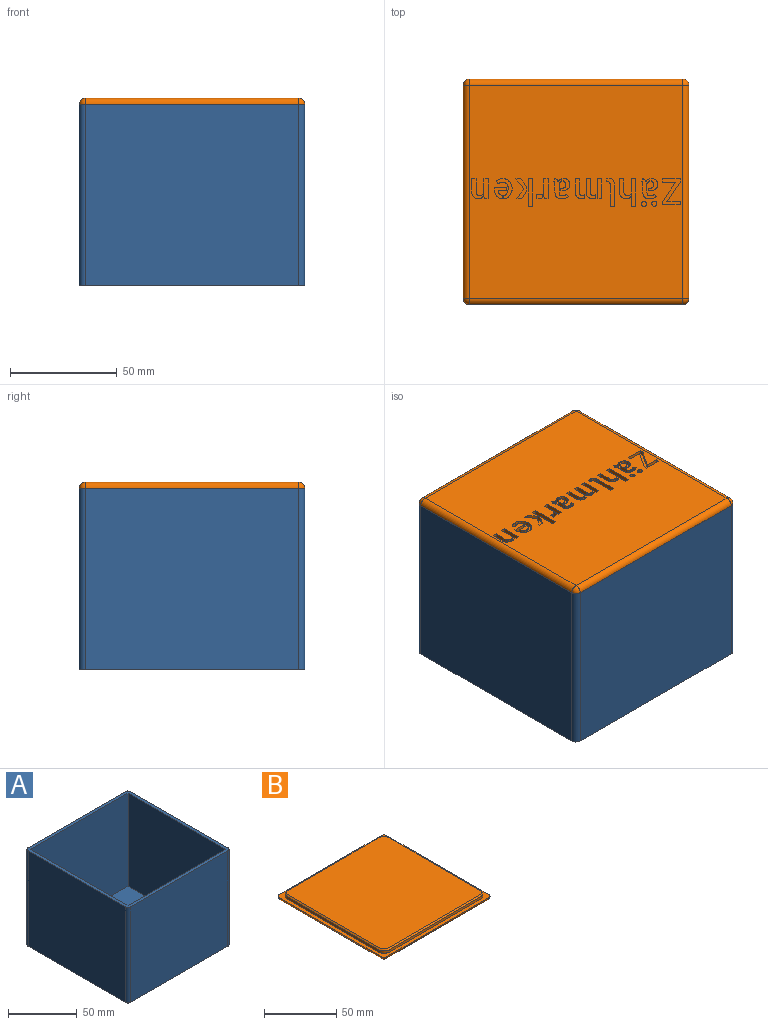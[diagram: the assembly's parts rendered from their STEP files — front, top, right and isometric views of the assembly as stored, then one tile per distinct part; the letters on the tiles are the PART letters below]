
ASSEMBLY  parts=2 mates=1
PART A: 15 faces, bbox 105.6x105.6x85 mm
  f0: plane 105.6x105.6mm, normal (0,0,-1), area 11144.6mm2, adj f5,f6,f7,f8,f9,f10,f11,f12
  f1: plane 100x83mm, normal (-1,0,0), area 8300mm2, adj f2,f4,f13,f14
  f2: plane 100x83mm, normal (0,-1,0), area 8300mm2, adj f1,f3,f13,f14
  f3: plane 100x83mm, normal (1,0,0), area 8300mm2, adj f2,f4,f13,f14
  f4: plane 100x83mm, normal (0,1,0), area 8300mm2, adj f1,f3,f13,f14
  f5: cylinder r=2.8mm len=85mm, axis (0,0,-1), area 373.8mm2, adj f0,f6,f12,f13
  f6: plane 100x85mm, normal (-1,0,0), area 8500mm2, adj f0,f5,f7,f13
  f7: cylinder r=2.8mm len=85mm, axis (0,0,-1), area 373.8mm2, adj f0,f6,f8,f13
  f8: plane 100x85mm, normal (0,-1,0), area 8500mm2, adj f0,f7,f9,f13
  f9: cylinder r=2.8mm len=85mm, axis (0,0,-1), area 373.8mm2, adj f0,f8,f10,f13
  f10: plane 100x85mm, normal (1,0,0), area 8500mm2, adj f0,f9,f11,f13
  f11: cylinder r=2.8mm len=85mm, axis (0,0,-1), area 373.8mm2, adj f0,f10,f12,f13
  f12: plane 100x85mm, normal (0,1,0), area 8500mm2, adj f0,f5,f11,f13
  f13: plane 105.6x105.6mm, normal (0,0,1), area 1144.6mm2, adj f1,f2,f3,f4,f5,f6,f7,f8
  f14: plane 100x100mm, normal (0,0,1), area 10000mm2, adj f1,f2,f3,f4
PART B: 344 faces, bbox 105.6x105.6x5.8 mm
  f0: extruded ~1.8x0.65mm, area 1.4mm2, adj f1,f295,f309,f323
  f1: extruded ~1.8x1.03mm, area 2.4mm2, adj f0,f2,f309,f323
  f2: extruded ~1.8x1.26mm, area 2.4mm2, adj f1,f3,f309,f323
  f3: extruded ~1.8x1.02mm, area 1.9mm2, adj f2,f4,f309,f323
  f4: extruded ~1.8x0.97mm, area 1.9mm2, adj f3,f5,f309,f323
  f5: plane 1.8x1.27mm, normal (-1,0,0), area 2.3mm2, adj f4,f6,f309,f323
  f6: extruded ~1.8x0.75mm, area 1.4mm2, adj f5,f7,f309,f323
  f7: extruded ~1.8x0.62mm, area 1.1mm2, adj f6,f8,f309,f323
  f8: extruded ~1.8x0.88mm, area 1.7mm2, adj f7,f9,f309,f323
  f9: extruded ~1.8x0.62mm, area 1.4mm2, adj f8,f10,f309,f323
  f10: extruded ~1.8x0.91mm, area 1.7mm2, adj f9,f11,f309,f323
  f11: extruded ~1.8x1.07mm, area 1.9mm2, adj f10,f12,f309,f323
  f12: plane 5.07x1.8mm, normal (-1,0,0), area 9.1mm2, adj f11,f13,f309,f323
  f13: plane 2.01x1.8mm, normal (0,1,0), area 3.6mm2, adj f12,f14,f309,f323
  f14: plane 5.24x1.8mm, normal (1,0,0), area 9.4mm2, adj f13,f15,f309,f323
  f15: extruded ~1.8x0.81mm, area 1.5mm2, adj f14,f16,f309,f323
  f16: extruded ~1.8x0.82mm, area 1.5mm2, adj f15,f295,f309,f323
  f17: plane 1.8x0.94mm, normal (0.98,-0.22,0), area 1.7mm2, adj f18,f275,f309,f343
  f18: plane 1.8x1.78mm, normal (0,-1,0), area 3.2mm2, adj f17,f19,f309,f343
  f19: plane 9.32x1.8mm, normal (-1,0,0), area 16.8mm2, adj f18,f20,f309,f343
  f20: plane 2x1.8mm, normal (0,1,0), area 3.6mm2, adj f19,f275,f309,f343
  f21: extruded ~1.8x0.45mm, area 0.8mm2, adj f22,f276,f309,f342
  f22: extruded ~1.8x1.18mm, area 2.2mm2, adj f21,f23,f309,f342
  f23: extruded ~1.8x0.82mm, area 1.9mm2, adj f22,f24,f309,f342
  f24: extruded ~1.8x0.96mm, area 1.9mm2, adj f23,f25,f309,f342
  f25: extruded ~1.8x1.2mm, area 2.2mm2, adj f24,f26,f309,f342
  f26: extruded ~1.8x0.88mm, area 1.6mm2, adj f25,f27,f309,f342
  f27: extruded ~1.8x1mm, area 1.9mm2, adj f26,f28,f309,f342
  f28: extruded ~1.8x0.87mm, area 1.9mm2, adj f27,f29,f309,f342
  f29: extruded ~1.8x1.01mm, area 2.1mm2, adj f28,f30,f309,f342
  f30: plane 1.8x1.59mm, normal (1,0,0), area 2.9mm2, adj f29,f31,f309,f342
  f31: extruded ~1.8x1.51mm, area 2.9mm2, adj f30,f32,f309,f342
  f32: extruded ~1.8x1.23mm, area 2.9mm2, adj f31,f33,f309,f342
  f33: extruded ~1.8x1.48mm, area 3.1mm2, adj f32,f34,f309,f342
  f34: extruded ~1.8x1.78mm, area 3.3mm2, adj f33,f35,f309,f342
  f35: extruded ~1.85x1.8mm, area 3.4mm2, adj f34,f36,f309,f342
  f36: extruded ~1.8x1.5mm, area 3.2mm2, adj f35,f37,f309,f342
  f37: extruded ~1.8x1.35mm, area 3.1mm2, adj f36,f38,f309,f342
  f38: extruded ~1.8x1.7mm, area 3.2mm2, adj f37,f39,f309,f342
  f39: extruded ~1.85x1.8mm, area 3.4mm2, adj f38,f40,f309,f342
  f40: extruded ~1.8x1.27mm, area 3mm2, adj f39,f41,f309,f342
  f41: plane 1.8x1.11mm, normal (0.84,-0.55,0), area 2.4mm2, adj f40,f42,f309,f342
  f42: extruded ~1.8x0.54mm, area 1.2mm2, adj f41,f43,f309,f342
  f43: extruded ~1.8x0.61mm, area 1.2mm2, adj f42,f276,f309,f342
  f44: extruded ~1.8x1.61mm, area 3mm2, adj f45,f277,f309,f341
  f45: plane 1.8x1.55mm, normal (-1,0,0), area 2.8mm2, adj f44,f46,f309,f341
  f46: extruded ~1.8x0.81mm, area 1.6mm2, adj f45,f47,f309,f341
  f47: extruded ~1.8x0.64mm, area 1.5mm2, adj f46,f48,f309,f341
  f48: extruded ~1.8x0.73mm, area 1.5mm2, adj f47,f49,f309,f341
  f49: extruded ~1.8x0.83mm, area 1.5mm2, adj f48,f50,f309,f341
  f50: plane 3.81x1.8mm, normal (0,-1,0), area 6.9mm2, adj f49,f51,f309,f341
  f51: plane 1.8x1.45mm, normal (-1,0,0), area 2.6mm2, adj f50,f52,f309,f341
  f52: plane 5.66x1.8mm, normal (0,1,0), area 10.2mm2, adj f51,f53,f309,f341
  f53: extruded ~1.8x0.79mm, area 1.4mm2, adj f52,f54,f309,f341
  f54: extruded ~1.8x1.69mm, area 3.1mm2, adj f53,f55,f309,f341
  f55: extruded ~1.8x1.44mm, area 3mm2, adj f54,f277,f309,f341
  f56: plane 12.84x1.8mm, normal (-1,0,0), area 23.1mm2, adj f57,f278,f309,f340
  f57: plane 2.01x1.8mm, normal (0,1,0), area 3.6mm2, adj f56,f58,f309,f340
  f58: plane 12.84x1.8mm, normal (1,0,0), area 23.1mm2, adj f57,f278,f309,f340
  f59: plane 4.68x3.7mm, normal (0.78,-0.62,0), area 10.7mm2, adj f60,f279,f309,f339
  f60: plane 4.64x3.27mm, normal (0.82,0.58,0), area 10.2mm2, adj f59,f61,f309,f339
  f61: plane 2.25x1.8mm, normal (0,-1,0), area 4mm2, adj f60,f62,f309,f339
  f62: plane 3.45x2.31mm, normal (-0.83,-0.56,0), area 7.5mm2, adj f61,f63,f309,f339
  f63: plane 2.3x1.8mm, normal (-1,0,0), area 4.1mm2, adj f62,f64,f309,f339
  f64: plane 3.57x2.71mm, normal (-0.8,0.6,0), area 8.1mm2, adj f63,f279,f309,f339
  f65: extruded ~1.8x0.99mm, area 1.9mm2, adj f66,f280,f309,f338
  f66: plane 1.8x1.69mm, normal (-1,0,0), area 3mm2, adj f65,f67,f309,f338
  f67: extruded ~1.8x0.7mm, area 1.3mm2, adj f66,f68,f309,f338
  f68: extruded ~1.8x0.74mm, area 1.3mm2, adj f67,f69,f309,f338
  f69: extruded ~1.8x1.12mm, area 2mm2, adj f68,f70,f309,f338
  f70: plane 2.08x1.8mm, normal (1,0,0), area 3.7mm2, adj f69,f280,f309,f338
  f71: plane 1.8x0.96mm, normal (0.98,-0.22,0), area 1.8mm2, adj f72,f281,f309,f337
  f72: plane 1.8x1.78mm, normal (0,-1,0), area 3.2mm2, adj f71,f73,f309,f337
  f73: plane 9.32x1.8mm, normal (-1,0,0), area 16.8mm2, adj f72,f74,f309,f337
  f74: plane 2x1.8mm, normal (0,1,0), area 3.6mm2, adj f73,f281,f309,f337
  f75: extruded ~1.8x0.39mm, area 0.7mm2, adj f76,f282,f309,f336
  f76: plane 2.28x1.8mm, normal (1,0,0), area 4.1mm2, adj f75,f77,f309,f336
  f77: extruded ~1.8x1.17mm, area 2.1mm2, adj f76,f78,f309,f336
  f78: extruded ~1.8x1.17mm, area 2.1mm2, adj f77,f79,f309,f336
  f79: extruded ~1.8x0.96mm, area 1.9mm2, adj f78,f80,f309,f336
  f80: extruded ~1.8x0.68mm, area 1.7mm2, adj f79,f81,f309,f336
  f81: extruded ~1.8x0.86mm, area 1.7mm2, adj f80,f82,f309,f336
  f82: extruded ~1.8x0.97mm, area 1.8mm2, adj f81,f83,f309,f336
  f83: extruded ~1.8x1.05mm, area 1.9mm2, adj f82,f84,f309,f336
  f84: extruded ~1.8x0.93mm, area 1.7mm2, adj f83,f85,f309,f336
  f85: extruded ~1.8x0.76mm, area 1.5mm2, adj f84,f86,f309,f336
  f86: extruded ~1.8x0.49mm, area 1.1mm2, adj f85,f87,f309,f336
  f87: plane 1.8x1.14mm, normal (-0.84,0.55,0), area 2.4mm2, adj f86,f88,f309,f336
  f88: extruded ~1.8x0.31mm, area 0.7mm2, adj f87,f89,f309,f336
  f89: extruded ~1.8x0.48mm, area 1mm2, adj f88,f90,f309,f336
  f90: extruded ~1.8x0.59mm, area 1.1mm2, adj f89,f91,f309,f336
  f91: extruded ~1.8x0.68mm, area 1.2mm2, adj f90,f92,f309,f336
  f92: extruded ~1.8x0.69mm, area 1.2mm2, adj f91,f93,f309,f336
  f93: extruded ~1.8x0.49mm, area 1mm2, adj f92,f94,f309,f336
  f94: extruded ~1.8x0.7mm, area 1.4mm2, adj f93,f95,f309,f336
  f95: extruded ~1.8x1.29mm, area 2.3mm2, adj f94,f96,f309,f336
  f96: plane 3.49x1.8mm, normal (-1,0,0), area 6.3mm2, adj f95,f97,f309,f336
  f97: extruded ~1.8x0.57mm, area 1.4mm2, adj f96,f98,f309,f336
  f98: extruded ~1.8x0.72mm, area 1.4mm2, adj f97,f99,f309,f336
  f99: plane 1.8x1.26mm, normal (-1,0,0), area 2.3mm2, adj f98,f100,f309,f336
  f100: extruded ~1.8x1.08mm, area 2.1mm2, adj f99,f101,f309,f336
  f101: extruded ~1.8x0.73mm, area 1.8mm2, adj f100,f102,f309,f336
  f102: extruded ~1.8x0.49mm, area 1mm2, adj f101,f103,f309,f336
  f103: extruded ~1.8x0.4mm, area 1mm2, adj f102,f104,f309,f336
  f104: extruded ~1.8x0.46mm, area 1mm2, adj f103,f105,f309,f336
  f105: extruded ~1.8x0.45mm, area 0.8mm2, adj f104,f106,f309,f336
  f106: plane 1.8x1.11mm, normal (0.9,0.43,0), area 2.2mm2, adj f105,f107,f309,f336
  f107: extruded ~1.8x0.29mm, area 0.7mm2, adj f106,f108,f309,f336
  f108: extruded ~1.8x0.48mm, area 0.9mm2, adj f107,f282,f309,f336
  f109: extruded ~1.8x1.11mm, area 2.1mm2, adj f110,f283,f309,f335
  f110: extruded ~1.8x0.87mm, area 1.6mm2, adj f109,f111,f309,f335
  f111: extruded ~1.8x0.52mm, area 1.3mm2, adj f110,f112,f309,f335
  f112: extruded ~1.8x0.68mm, area 1.3mm2, adj f111,f113,f309,f335
  f113: extruded ~1.8x0.69mm, area 1.3mm2, adj f112,f114,f309,f335
  f114: plane 1.8x0.36mm, normal (0,1,0), area 0.7mm2, adj f113,f115,f309,f335
  f115: plane 1.8x1.17mm, normal (1,0,0), area 2.1mm2, adj f114,f116,f309,f335
  f116: plane 1.8x0.73mm, normal (0,-1,0), area 1.3mm2, adj f115,f117,f309,f335
  f117: extruded ~1.8x1.3mm, area 2.4mm2, adj f116,f118,f309,f335
  f118: extruded ~1.8x1.15mm, area 2.3mm2, adj f117,f119,f309,f335
  f119: extruded ~1.8x0.91mm, area 2.2mm2, adj f118,f120,f309,f335
  f120: extruded ~1.8x1.31mm, area 2.5mm2, adj f119,f121,f309,f335
  f121: extruded ~1.8x1.34mm, area 2.5mm2, adj f120,f122,f309,f335
  f122: extruded ~1.8x0.88mm, area 2mm2, adj f121,f123,f309,f335
  f123: extruded ~1.8x0.92mm, area 1.9mm2, adj f122,f124,f309,f335
  f124: extruded ~1.8x1.08mm, area 2mm2, adj f123,f125,f309,f335
  f125: extruded ~1.8x0.21mm, area 0.4mm2, adj f124,f126,f309,f335
  f126: plane 1.8x1.34mm, normal (1,0,0), area 2.4mm2, adj f125,f283,f309,f335
  f127: extruded ~1.8x0.63mm, area 1.3mm2, adj f128,f284,f309,f334
  f128: extruded ~1.8x1.02mm, area 2.5mm2, adj f127,f129,f309,f334
  f129: extruded ~1.8x1.28mm, area 2.4mm2, adj f128,f130,f309,f334
  f130: extruded ~1.8x0.9mm, area 1.7mm2, adj f129,f131,f309,f334
  f131: extruded ~1.8x0.85mm, area 1.7mm2, adj f130,f132,f309,f334
  f132: plane 1.8x1.31mm, normal (-1,0,0), area 2.4mm2, adj f131,f133,f309,f334
  f133: extruded ~1.8x0.77mm, area 1.5mm2, adj f132,f134,f309,f334
  f134: extruded ~1.8x0.59mm, area 1.1mm2, adj f133,f135,f309,f334
  f135: extruded ~1.8x0.68mm, area 1.3mm2, adj f134,f136,f309,f334
  f136: extruded ~1.8x0.62mm, area 1.3mm2, adj f135,f137,f309,f334
  f137: extruded ~1.8x0.9mm, area 1.6mm2, adj f136,f138,f309,f334
  f138: plane 6.14x1.8mm, normal (-1,0,0), area 11mm2, adj f137,f139,f309,f334
  f139: plane 2x1.8mm, normal (0,1,0), area 3.6mm2, adj f138,f140,f309,f334
  f140: plane 5.24x1.8mm, normal (1,0,0), area 9.4mm2, adj f139,f141,f309,f334
  f141: extruded ~1.8x0.82mm, area 1.5mm2, adj f140,f142,f309,f334
  f142: extruded ~1.8x0.75mm, area 1.4mm2, adj f141,f284,f309,f334
  f143: extruded ~1.8x1.06mm, area 2mm2, adj f144,f285,f309,f333
  f144: extruded ~1.8x0.86mm, area 1.6mm2, adj f143,f145,f309,f333
  f145: extruded ~1.8x0.91mm, area 1.8mm2, adj f144,f146,f309,f333
  f146: plane 1.8x1.31mm, normal (-1,0,0), area 2.4mm2, adj f145,f147,f309,f333
  f147: extruded ~1.8x0.88mm, area 1.7mm2, adj f146,f148,f309,f333
  f148: extruded ~1.8x0.5mm, area 0.9mm2, adj f147,f149,f309,f333
  f149: extruded ~1.8x0.69mm, area 1.3mm2, adj f148,f150,f309,f333
  f150: extruded ~1.8x0.62mm, area 1.3mm2, adj f149,f151,f309,f333
  f151: extruded ~1.8x0.9mm, area 1.6mm2, adj f150,f152,f309,f333
  f152: extruded ~1.8x1.07mm, area 1.9mm2, adj f151,f153,f309,f333
  f153: plane 5.07x1.8mm, normal (-1,0,0), area 9.1mm2, adj f152,f154,f309,f333
  f154: plane 1.98x1.8mm, normal (0,1,0), area 3.6mm2, adj f153,f155,f309,f333
  f155: plane 6.34x1.8mm, normal (1,0,0), area 11.4mm2, adj f154,f156,f309,f333
  f156: extruded ~1.8x1.23mm, area 2.3mm2, adj f155,f157,f309,f333
  f157: extruded ~1.8x0.98mm, area 2.1mm2, adj f156,f285,f309,f333
  f158: plane 1.8x0.96mm, normal (0.98,-0.22,0), area 1.8mm2, adj f159,f286,f309,f332
  f159: plane 1.8x1.8mm, normal (0,-1,0), area 3.2mm2, adj f158,f160,f309,f332
  f160: plane 9.32x1.8mm, normal (-1,0,0), area 16.8mm2, adj f159,f161,f309,f332
  f161: plane 2.01x1.8mm, normal (0,1,0), area 3.6mm2, adj f160,f286,f309,f332
  f162: extruded ~1.8x0.88mm, area 1.6mm2, adj f163,f287,f309,f331
  f163: plane 9.99x1.8mm, normal (1,0,0), area 18mm2, adj f162,f164,f309,f331
  f164: plane 2.02x1.8mm, normal (0,-1,0), area 3.6mm2, adj f163,f165,f309,f331
  f165: plane 9.89x1.8mm, normal (-1,0,0), area 17.8mm2, adj f164,f166,f309,f331
  f166: extruded ~1.8x0.7mm, area 1.3mm2, adj f165,f167,f309,f331
  f167: extruded ~1.8x0.92mm, area 1.7mm2, adj f166,f168,f309,f331
  f168: extruded ~1.8x0.85mm, area 1.8mm2, adj f167,f169,f309,f331
  f169: extruded ~1.8x0.88mm, area 1.8mm2, adj f168,f170,f309,f331
  f170: extruded ~1.8x0.45mm, area 0.8mm2, adj f169,f171,f309,f331
  f171: extruded ~1.8x0.5mm, area 0.9mm2, adj f170,f172,f309,f331
  f172: extruded ~1.8x0.49mm, area 0.9mm2, adj f171,f173,f309,f331
  f173: extruded ~1.8x0.43mm, area 0.8mm2, adj f172,f174,f309,f331
  f174: extruded ~1.8x0.44mm, area 0.8mm2, adj f173,f175,f309,f331
  f175: plane 1.8x1.22mm, normal (1,0,0), area 2.2mm2, adj f174,f176,f309,f331
  f176: extruded ~1.8x0.73mm, area 1.3mm2, adj f175,f177,f309,f331
  f177: extruded ~1.8x0.6mm, area 1.2mm2, adj f176,f287,f309,f331
  f178: extruded ~1.8x0.65mm, area 1.4mm2, adj f179,f288,f309,f330
  f179: extruded ~1.8x1.03mm, area 2.4mm2, adj f178,f180,f309,f330
  f180: extruded ~1.8x1.26mm, area 2.4mm2, adj f179,f181,f309,f330
  f181: extruded ~1.8x1.02mm, area 1.9mm2, adj f180,f182,f309,f330
  f182: extruded ~1.8x0.97mm, area 1.9mm2, adj f181,f183,f309,f330
  f183: plane 1.8x1.27mm, normal (-1,0,0), area 2.3mm2, adj f182,f184,f309,f330
  f184: extruded ~1.8x0.75mm, area 1.4mm2, adj f183,f185,f309,f330
  f185: extruded ~1.8x0.62mm, area 1.1mm2, adj f184,f186,f309,f330
  f186: extruded ~1.8x0.88mm, area 1.7mm2, adj f185,f187,f309,f330
  f187: extruded ~1.8x0.62mm, area 1.4mm2, adj f186,f188,f309,f330
  f188: extruded ~1.8x0.91mm, area 1.7mm2, adj f187,f189,f309,f330
  f189: extruded ~1.8x1.07mm, area 1.9mm2, adj f188,f190,f309,f330
  f190: plane 5.07x1.8mm, normal (-1,0,0), area 9.1mm2, adj f189,f191,f309,f330
  f191: plane 2.01x1.8mm, normal (0,1,0), area 3.6mm2, adj f190,f192,f309,f330
  f192: plane 5.24x1.8mm, normal (1,0,0), area 9.4mm2, adj f191,f193,f309,f330
  f193: extruded ~1.8x0.81mm, area 1.5mm2, adj f192,f194,f309,f330
  f194: extruded ~1.8x0.82mm, area 1.5mm2, adj f193,f288,f309,f330
  f195: plane 2x1.8mm, normal (0,-1,0), area 3.6mm2, adj f196,f289,f309,f329
  f196: plane 12.84x1.8mm, normal (-1,0,0), area 23.1mm2, adj f195,f197,f309,f329
  f197: plane 2x1.8mm, normal (0,1,0), area 3.6mm2, adj f196,f289,f309,f329
  f198: extruded ~1.8x0.84mm, area 1.7mm2, adj f199,f290,f309,f328
  f199: extruded ~1.8x0.83mm, area 1.7mm2, adj f198,f200,f309,f328
  f200: extruded ~1.8x0.84mm, area 1.7mm2, adj f199,f201,f309,f328
  f201: extruded ~1.8x0.84mm, area 1.7mm2, adj f200,f202,f309,f328
  f202: extruded ~1.8x0.83mm, area 1.7mm2, adj f201,f203,f309,f328
  f203: extruded ~1.8x0.84mm, area 1.7mm2, adj f202,f204,f309,f328
  f204: extruded ~1.8x0.84mm, area 1.7mm2, adj f203,f290,f309,f328
  f205: extruded ~1.8x0.84mm, area 1.7mm2, adj f206,f291,f309,f327
  f206: extruded ~1.8x0.83mm, area 1.7mm2, adj f205,f207,f309,f327
  f207: extruded ~1.8x0.84mm, area 1.7mm2, adj f206,f208,f309,f327
  f208: extruded ~1.8x0.84mm, area 1.7mm2, adj f207,f209,f309,f327
  f209: extruded ~1.8x0.83mm, area 1.7mm2, adj f208,f210,f309,f327
  f210: extruded ~1.8x0.84mm, area 1.7mm2, adj f209,f211,f309,f327
  f211: extruded ~1.8x0.84mm, area 1.7mm2, adj f210,f291,f309,f327
  f212: extruded ~1.8x0.39mm, area 0.7mm2, adj f213,f292,f309,f326
  f213: plane 2.28x1.8mm, normal (1,0,0), area 4.1mm2, adj f212,f214,f309,f326
  f214: extruded ~1.8x1.17mm, area 2.1mm2, adj f213,f215,f309,f326
  f215: extruded ~1.8x1.17mm, area 2.1mm2, adj f214,f216,f309,f326
  f216: extruded ~1.8x0.96mm, area 1.9mm2, adj f215,f217,f309,f326
  f217: extruded ~1.8x0.68mm, area 1.7mm2, adj f216,f218,f309,f326
  f218: extruded ~1.8x0.86mm, area 1.7mm2, adj f217,f219,f309,f326
  f219: extruded ~1.8x0.97mm, area 1.8mm2, adj f218,f220,f309,f326
  f220: extruded ~1.8x1.05mm, area 1.9mm2, adj f219,f221,f309,f326
  f221: extruded ~1.8x0.93mm, area 1.7mm2, adj f220,f222,f309,f326
  f222: extruded ~1.8x0.76mm, area 1.5mm2, adj f221,f223,f309,f326
  f223: extruded ~1.8x0.49mm, area 1.1mm2, adj f222,f224,f309,f326
  f224: plane 1.8x1.14mm, normal (-0.84,0.55,0), area 2.4mm2, adj f223,f225,f309,f326
  f225: extruded ~1.8x0.31mm, area 0.7mm2, adj f224,f226,f309,f326
  f226: extruded ~1.8x0.48mm, area 1mm2, adj f225,f227,f309,f326
  f227: extruded ~1.8x0.59mm, area 1.1mm2, adj f226,f228,f309,f326
  f228: extruded ~1.8x0.68mm, area 1.2mm2, adj f227,f229,f309,f326
  f229: extruded ~1.8x0.69mm, area 1.2mm2, adj f228,f230,f309,f326
  f230: extruded ~1.8x0.49mm, area 1mm2, adj f229,f231,f309,f326
  f231: extruded ~1.8x0.7mm, area 1.4mm2, adj f230,f232,f309,f326
  f232: extruded ~1.8x1.29mm, area 2.3mm2, adj f231,f233,f309,f326
  f233: plane 3.49x1.8mm, normal (-1,0,0), area 6.3mm2, adj f232,f234,f309,f326
  f234: extruded ~1.8x0.57mm, area 1.4mm2, adj f233,f235,f309,f326
  f235: extruded ~1.8x0.72mm, area 1.4mm2, adj f234,f236,f309,f326
  f236: plane 1.8x1.26mm, normal (-1,0,0), area 2.3mm2, adj f235,f237,f309,f326
  f237: extruded ~1.8x1.08mm, area 2.1mm2, adj f236,f238,f309,f326
  f238: extruded ~1.8x0.73mm, area 1.8mm2, adj f237,f239,f309,f326
  f239: extruded ~1.8x0.49mm, area 1mm2, adj f238,f240,f309,f326
  f240: extruded ~1.8x0.4mm, area 1mm2, adj f239,f241,f309,f326
  f241: extruded ~1.8x0.46mm, area 1mm2, adj f240,f242,f309,f326
  f242: extruded ~1.8x0.45mm, area 0.8mm2, adj f241,f243,f309,f326
  f243: plane 1.8x1.11mm, normal (0.9,0.43,0), area 2.2mm2, adj f242,f244,f309,f326
  f244: extruded ~1.8x0.29mm, area 0.7mm2, adj f243,f245,f309,f326
  f245: extruded ~1.8x0.48mm, area 0.9mm2, adj f244,f292,f309,f326
  f246: extruded ~1.8x1.11mm, area 2.1mm2, adj f247,f293,f309,f325
  f247: extruded ~1.8x0.87mm, area 1.6mm2, adj f246,f248,f309,f325
  f248: extruded ~1.8x0.52mm, area 1.3mm2, adj f247,f249,f309,f325
  f249: extruded ~1.8x0.68mm, area 1.3mm2, adj f248,f250,f309,f325
  f250: extruded ~1.8x0.69mm, area 1.3mm2, adj f249,f251,f309,f325
  f251: plane 1.8x0.36mm, normal (0,1,0), area 0.7mm2, adj f250,f252,f309,f325
  f252: plane 1.8x1.17mm, normal (1,0,0), area 2.1mm2, adj f251,f253,f309,f325
  f253: plane 1.8x0.73mm, normal (0,-1,0), area 1.3mm2, adj f252,f254,f309,f325
  f254: extruded ~1.8x1.3mm, area 2.4mm2, adj f253,f255,f309,f325
  f255: extruded ~1.8x1.15mm, area 2.3mm2, adj f254,f256,f309,f325
  f256: extruded ~1.8x0.91mm, area 2.2mm2, adj f255,f257,f309,f325
  f257: extruded ~1.8x1.31mm, area 2.5mm2, adj f256,f258,f309,f325
  f258: extruded ~1.8x1.34mm, area 2.5mm2, adj f257,f259,f309,f325
  f259: extruded ~1.8x0.88mm, area 2mm2, adj f258,f260,f309,f325
  f260: extruded ~1.8x0.92mm, area 1.9mm2, adj f259,f261,f309,f325
  f261: extruded ~1.8x1.08mm, area 2mm2, adj f260,f262,f309,f325
  f262: extruded ~1.8x0.21mm, area 0.4mm2, adj f261,f263,f309,f325
  f263: plane 1.8x1.34mm, normal (1,0,0), area 2.4mm2, adj f262,f293,f309,f325
  f264: plane 1.8x1.6mm, normal (1,0,0), area 2.9mm2, adj f265,f294,f309,f324
  f265: plane 8.09x1.8mm, normal (0,-1,0), area 14.6mm2, adj f264,f266,f309,f324
  f266: plane 1.8x1.6mm, normal (-1,0,0), area 2.9mm2, adj f265,f267,f309,f324
  f267: plane 6.15x1.8mm, normal (0,1,0), area 11.1mm2, adj f266,f268,f309,f324
  f268: plane 1.8x0.35mm, normal (-0.6,-0.8,0), area 0.8mm2, adj f267,f269,f309,f324
  f269: plane 8.71x5.8mm, normal (-0.83,-0.55,0), area 18.8mm2, adj f268,f270,f309,f324
  f270: plane 1.8x1.6mm, normal (-1,0,0), area 2.9mm2, adj f269,f271,f309,f324
  f271: plane 8.09x1.8mm, normal (0,1,0), area 14.6mm2, adj f270,f272,f309,f324
  f272: plane 1.8x1.6mm, normal (1,0,0), area 2.9mm2, adj f271,f273,f309,f324
  f273: plane 6.13x1.8mm, normal (0,-1,0), area 11mm2, adj f272,f274,f309,f324
  f274: plane 1.8x0.33mm, normal (0.62,0.78,0), area 0.8mm2, adj f273,f294,f309,f324
  f275: plane 8.38x1.8mm, normal (1,0,0), area 15.1mm2, adj f17,f20,f309,f343
  f276: extruded ~1.8x0.58mm, area 1.1mm2, adj f21,f43,f309,f342
  f277: extruded ~1.8x1.23mm, area 2.9mm2, adj f44,f55,f309,f341
  f278: plane 2.01x1.8mm, normal (0,-1,0), area 3.6mm2, adj f56,f58,f309,f340
  f279: plane 2.28x1.8mm, normal (0,1,0), area 4.1mm2, adj f59,f64,f309,f339
  f280: extruded ~1.8x1.57mm, area 2.8mm2, adj f65,f70,f309,f338
  f281: plane 8.36x1.8mm, normal (1,0,0), area 15mm2, adj f71,f74,f309,f337
  f282: extruded ~1.8x0.52mm, area 0.9mm2, adj f75,f108,f309,f336
  f283: extruded ~1.8x0.88mm, area 1.8mm2, adj f109,f126,f309,f335
  f284: extruded ~1.8x0.7mm, area 1.3mm2, adj f127,f142,f309,f334
  f285: extruded ~1.8x0.87mm, area 2mm2, adj f143,f157,f309,f333
  f286: plane 8.36x1.8mm, normal (1,0,0), area 15mm2, adj f158,f161,f309,f332
  f287: extruded ~1.8x0.48mm, area 1.2mm2, adj f162,f177,f309,f331
  f288: extruded ~1.8x0.78mm, area 1.5mm2, adj f178,f194,f309,f330
  f289: plane 12.84x1.8mm, normal (1,0,0), area 23.1mm2, adj f195,f197,f309,f329
  f290: extruded ~1.8x0.84mm, area 1.7mm2, adj f198,f204,f309,f328
  f291: extruded ~1.8x0.84mm, area 1.7mm2, adj f205,f211,f309,f327
  f292: extruded ~1.8x0.52mm, area 0.9mm2, adj f212,f245,f309,f326
  f293: extruded ~1.8x0.88mm, area 1.8mm2, adj f246,f263,f309,f325
  f294: plane 8.71x5.8mm, normal (0.83,0.55,0), area 18.8mm2, adj f264,f274,f309,f324
  f295: extruded ~1.8x0.78mm, area 1.5mm2, adj f0,f16,f309,f323
  f296: plane 105.6x105.6mm, normal (0,0,1), area 1166.1mm2, adj f297,f298,f299,f300,f301,f302,f303,f304
  f297: sphere r=2.8mm, area 12.3mm2, adj f296,f301,f305
  f298: sphere r=2.8mm, area 12.3mm2, adj f296,f303,f305
  f299: sphere r=2.8mm, area 12.3mm2, adj f296,f301,f307
  f300: sphere r=2.8mm, area 12.3mm2, adj f296,f303,f307
  f301: cylinder r=2.8mm len=100mm, axis (0,-1,0), area 439.8mm2, adj f296,f297,f299,f309
  f302: plane 90x2mm, normal (-1,0,0), area 180mm2, adj f296,f312,f313,f315
  f303: cylinder r=2.8mm len=100mm, axis (0,-1,0), area 439.8mm2, adj f296,f298,f300,f309
  f304: plane 90x2mm, normal (1,0,0), area 180mm2, adj f296,f311,f314,f322
  f305: cylinder r=2.8mm len=100mm, axis (-1,0,0), area 439.8mm2, adj f296,f297,f298,f309
  f306: plane 90x2mm, normal (0,-1,0), area 180mm2, adj f296,f313,f314,f319
  f307: cylinder r=2.8mm len=100mm, axis (-1,0,0), area 439.8mm2, adj f296,f299,f300,f309
  f308: plane 90x2mm, normal (0,1,0), area 180mm2, adj f296,f311,f312,f318
  f309: plane 100x100mm, normal (0,0,-1), area 9587.6mm2, adj f0,f1,f2,f3,f4,f5,f6,f7
  f310: plane 98x98mm, normal (0,0,1), area 9590.3mm2, adj f315,f316,f317,f318,f319,f320,f321,f322
  f311: cylinder r=5mm len=5mm, axis (0,0,1), area 15.7mm2, adj f296,f304,f308,f320
  f312: cylinder r=5mm len=5mm, axis (0,0,-1), area 15.7mm2, adj f296,f302,f308,f316
  f313: cylinder r=5mm len=5mm, axis (0,0,1), area 15.7mm2, adj f296,f302,f306,f317
  f314: cylinder r=5mm len=5mm, axis (0,0,-1), area 15.7mm2, adj f296,f304,f306,f321
  f315: plane 90x1mm, normal (-0.71,0,0.71), area 127.3mm2, adj f302,f310,f316,f317
  f316: cone r=4mm half-angle=45deg, axis (0,0,-1), area 10mm2, adj f310,f312,f315,f318
  f317: cone r=4mm half-angle=45deg, axis (0,0,-1), area 10mm2, adj f310,f313,f315,f319
  f318: plane 90x1mm, normal (0,0.71,0.71), area 127.3mm2, adj f308,f310,f316,f320
  f319: plane 90x1mm, normal (0,-0.71,0.71), area 127.3mm2, adj f306,f310,f317,f321
  f320: cone r=4mm half-angle=45deg, axis (0,0,-1), area 10mm2, adj f310,f311,f318,f322
  f321: cone r=4mm half-angle=45deg, axis (0,0,-1), area 10mm2, adj f310,f314,f319,f322
  f322: plane 90x1mm, normal (0.71,0,0.71), area 127.3mm2, adj f304,f310,f320,f321
  f323: plane 9.42x5.04mm, normal (0,0,-1), area 21.8mm2, adj f0,f1,f2,f3,f4,f5,f6,f7
  f324: plane 12.17x8.09mm, normal (0,0,-1), area 44.9mm2, adj f264,f265,f266,f267,f268,f269,f270,f271
  f325: plane 5.76x4.33mm, normal (0,0,-1), area 12.7mm2, adj f246,f247,f248,f249,f250,f251,f252,f253
  f326: plane 9.4x6.87mm, normal (0,0,-1), area 24.2mm2, adj f212,f213,f214,f215,f216,f217,f218,f219
  f327: plane 2.38x2.36mm, normal (0,0,-1), area 4.4mm2, adj f205,f206,f207,f208,f209,f210,f211,f291
  f328: plane 2.38x2.36mm, normal (0,0,-1), area 4.4mm2, adj f198,f199,f200,f201,f202,f203,f204,f290
  f329: plane 12.84x2mm, normal (0,0,-1), area 25.6mm2, adj f195,f196,f197,f289
  f330: plane 9.42x5.04mm, normal (0,0,-1), area 21.8mm2, adj f178,f179,f180,f181,f182,f183,f184,f185
  f331: plane 12.92x3.91mm, normal (0,0,-1), area 27.8mm2, adj f162,f163,f164,f165,f166,f167,f168,f169
  f332: plane 9.32x2.01mm, normal (0,0,-1), area 18.7mm2, adj f158,f159,f160,f161,f286
  f333: plane 9.42x4.48mm, normal (0,0,-1), area 20.9mm2, adj f143,f144,f145,f146,f147,f148,f149,f150
  f334: plane 9.38x4.48mm, normal (0,0,-1), area 21mm2, adj f127,f128,f129,f130,f131,f132,f133,f134
  f335: plane 5.76x4.33mm, normal (0,0,-1), area 12.7mm2, adj f109,f110,f111,f112,f113,f114,f115,f116
  f336: plane 9.4x6.87mm, normal (0,0,-1), area 24.2mm2, adj f75,f76,f77,f78,f79,f80,f81,f82
  f337: plane 9.32x2mm, normal (0,0,-1), area 18.5mm2, adj f71,f72,f73,f74,f281
  f338: plane 2.56x2.16mm, normal (0,0,-1), area 4.8mm2, adj f65,f66,f67,f68,f69,f70,f280
  f339: plane 9.32x4.99mm, normal (0,0,-1), area 19.4mm2, adj f59,f60,f61,f62,f63,f64,f279
  f340: plane 12.84x2.01mm, normal (0,0,-1), area 25.9mm2, adj f56,f57,f58,f278
  f341: plane 5.71x5.42mm, normal (0,0,-1), area 16.1mm2, adj f44,f45,f46,f47,f48,f49,f50,f51
  f342: plane 9.48x7.4mm, normal (0,0,-1), area 24mm2, adj f21,f22,f23,f24,f25,f26,f27,f28
  f343: plane 9.32x2mm, normal (0,0,-1), area 18.5mm2, adj f17,f18,f19,f20,f275
PLACE A rot(axis=(0,0,1),0deg) t=(0,0,-42.5)mm fixed
PLACE B rot(axis=(1,0,0),180deg) t=(0.08,0.03,42.5)mm
MATE slider B.f309 <-> A.f14  axis (0,0,1) through (0,0,45.3)mm
